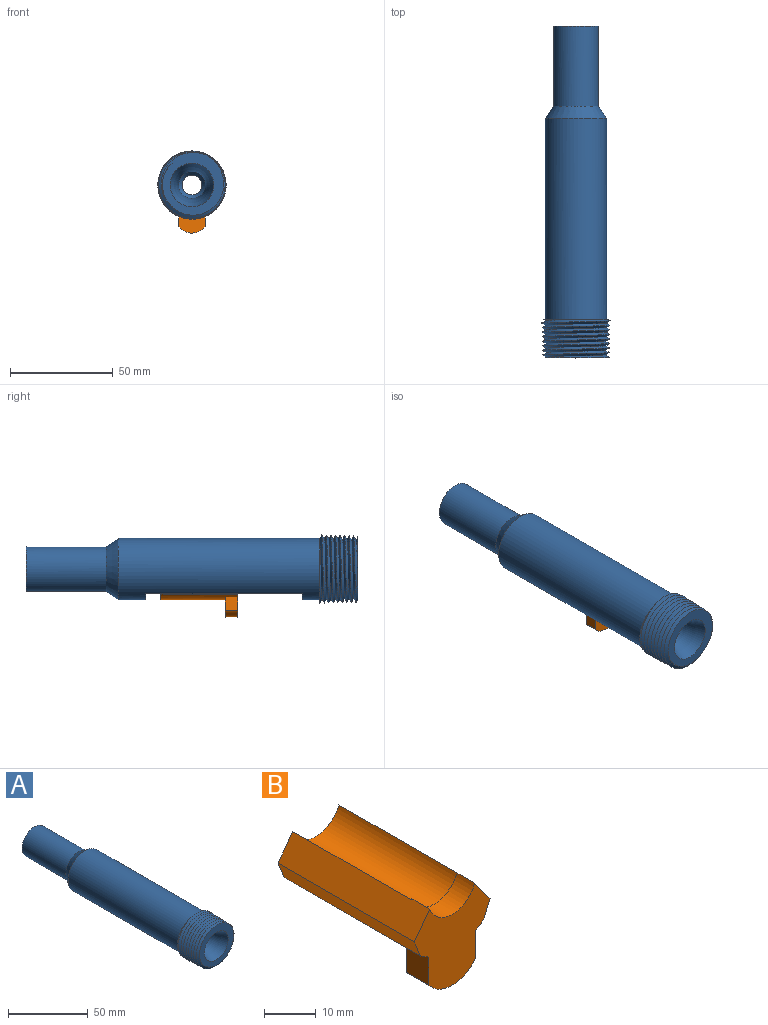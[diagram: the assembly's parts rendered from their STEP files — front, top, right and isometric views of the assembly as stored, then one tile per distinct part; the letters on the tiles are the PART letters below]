
ASSEMBLY  parts=2 mates=1
PART A: 26 faces, bbox 42.6x174.7x42.6 mm
  f0: cylinder r=4.8mm len=75.31mm, axis (0,-1,0), area 1899.9mm2, adj f2,f10,f16,f18,f25
  f1: cone r=14.87mm half-angle=34.1deg, axis (0,-1,0), area 573.2mm2, adj f3,f22
  f2: plane 12.48x6.54mm, normal (0,1,0), area 27.4mm2, adj f0,f16,f17,f18
  f3: cylinder r=14.87mm len=97.8mm, axis (0,-1,0), area 7681.7mm2, adj f1,f11,f12,f15,f19,f20,f21
  f4: cone r=14.87mm half-angle=1.6deg, axis (0,1,0), area 0.6mm2, adj f6,f8,f14
  f5: torus R=51.79mm, axis (0,-1,0), area 949.6mm2, adj f10,f14
  f6: bspline ~33.39x33.36mm, area 1702.7mm2, adj f4,f7,f11,f12,f13,f14
  f7: bspline ~33.38x33.36mm, area 1643.8mm2, adj f6,f9,f11,f12,f14
  f8: plane 0.18x0.05mm, normal (-0.71,0,0.71), area 0mm2, adj f4,f9,f13,f14
  f9: plane 0.8x0.67mm, normal (-0.64,0,-0.77), area 0.1mm2, adj f7,f8,f11,f13,f14
  f10: cone r=6.54mm half-angle=35.8deg, axis (0,-1,0), area 106.1mm2, adj f0,f5
  f11: cone r=14.87mm half-angle=1.6deg, axis (0,1,0), area 69.5mm2, adj f3,f6,f7,f9
  f12: plane 31.49x31.46mm, normal (0,1,0), area 82.5mm2, adj f3,f6,f7
  f13: plane 0.19x0.17mm, normal (0,-1,0), area 0mm2, adj f6,f8,f9
  f14: plane 30.44x30.41mm, normal (0,-1,0), area 376.2mm2, adj f4,f5,f6,f7,f8,f9
  f15: plane 75.95x4.01mm, normal (0.93,0,0.38), area 329.2mm2, adj f3,f16,f20,f21
  f16: plane 75.95x7.88mm, normal (0.81,0,-0.59), area 616.6mm2, adj f0,f2,f15,f17,f20,f21,f24,f25
  f17: cylinder r=6.54mm len=44.69mm, axis (0,1,0), area 740.2mm2, adj f2,f16,f18,f20
  f18: plane 75.95x7.88mm, normal (-0.81,0,-0.59), area 616.6mm2, adj f0,f2,f17,f19,f20,f21,f24,f25
  f19: plane 75.95x4.01mm, normal (-0.93,0,0.38), area 329.2mm2, adj f3,f18,f20,f21
  f20: plane 21.16x12.91mm, normal (0,1,0), area 172.1mm2, adj f3,f15,f16,f17,f18,f19
  f21: plane 21.16x12.85mm, normal (0,-1,0), area 171.1mm2, adj f3,f15,f16,f18,f19,f24
  f22: cylinder r=10.9mm len=38.85mm, axis (0,-1,0), area 2661.3mm2, adj f1,f23
  f23: plane 21.81x21.81mm, normal (0,1,0), area 236.6mm2, adj f22,f24
  f24: cylinder r=6.6mm len=64.8mm, axis (0,1,0), area 2576.8mm2, adj f16,f18,f21,f23,f25
  f25: plane 13.2x8.62mm, normal (0,1,0), area 36.1mm2, adj f0,f16,f18,f24
PART B: 14 faces, bbox 20.7x37.3x21.1 mm
  f0: plane 37.34x5.71mm, normal (0.81,0,0.59), area 256.7mm2, adj f1,f5,f6,f7,f8,f9
  f1: plane 37.34x4.21mm, normal (0.93,0,-0.38), area 169.8mm2, adj f0,f2,f6,f7
  f2: cylinder r=14.87mm len=37.34mm, axis (0,1,0), area 606.9mm2, adj f1,f3,f6,f7,f10,f11,f13
  f3: plane 37.34x4.21mm, normal (-0.93,0,-0.38), area 169.8mm2, adj f2,f4,f6,f7
  f4: plane 37.34x5.71mm, normal (-0.81,0,0.59), area 256.7mm2, adj f3,f5,f6,f7,f8,f9
  f5: cylinder r=6.54mm len=12.32mm, axis (0,1,0), area 78.4mm2, adj f0,f4,f6,f9
  f6: plane 21.14x20.7mm, normal (0,-1,0), area 268.7mm2, adj f0,f1,f2,f3,f4,f5,f10,f11
  f7: plane 20.7x12.48mm, normal (0,1,0), area 164.2mm2, adj f0,f1,f2,f3,f4,f8
  f8: cylinder r=6.74mm len=32.46mm, axis (0,1,0), area 528.9mm2, adj f0,f4,f7,f9
  f9: plane 12.61x4.55mm, normal (0,1,0), area 3.2mm2, adj f0,f4,f5,f8
  f10: plane 6.69x6.1mm, normal (1,0,0), area 40.8mm2, adj f2,f6,f12,f13
  f11: plane 6.69x6.1mm, normal (-1,0,0), area 40.8mm2, adj f2,f6,f12,f13
  f12: cylinder r=7.91mm len=12.71mm, axis (0,-1,0), area 90mm2, adj f6,f10,f11,f13
  f13: plane 12.71x9.89mm, normal (0,1,0), area 101.2mm2, adj f2,f10,f11,f12
PLACE A t=(-102.92,-223.1,-22.99)mm
PLACE B t=(-102.92,-229.68,-22.99)mm
MATE slider B.f8 <-> A.f22  axis (0,-1,0) through (-102.92,-51.83,8.98)mm
